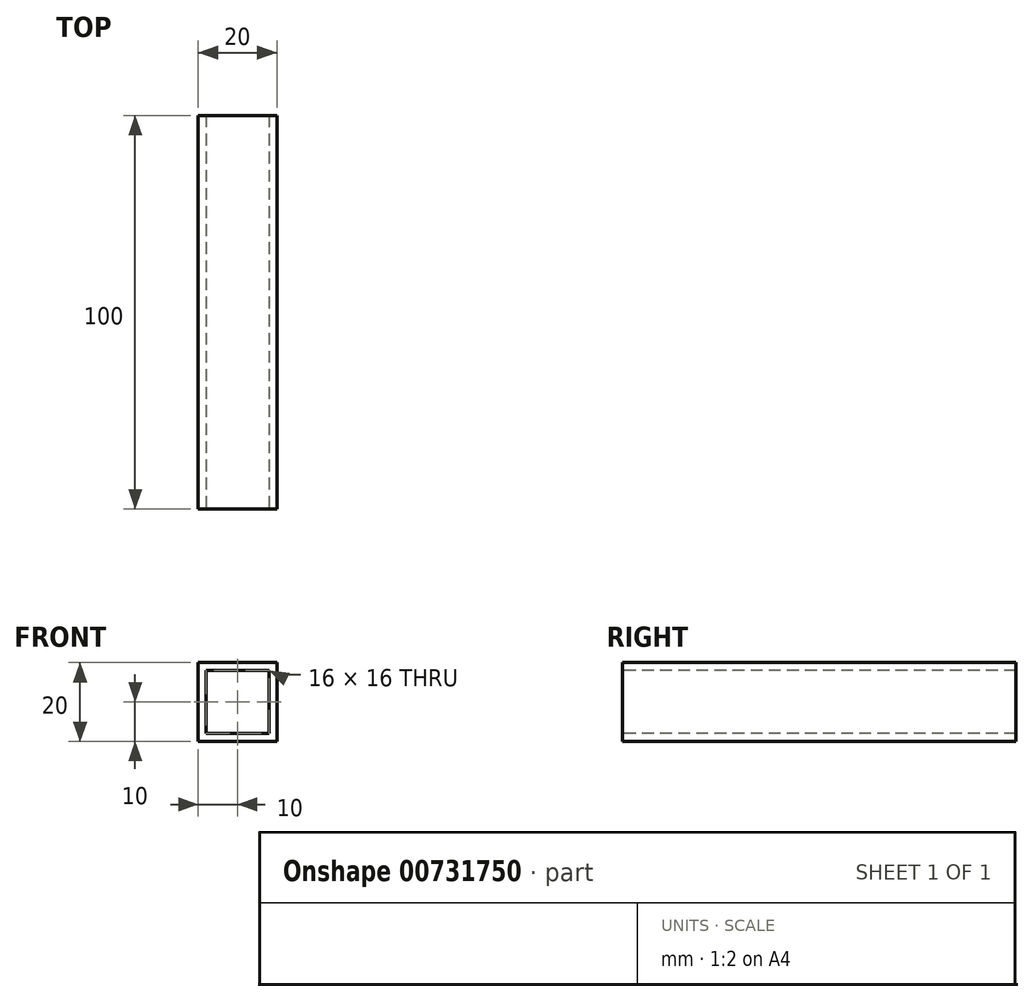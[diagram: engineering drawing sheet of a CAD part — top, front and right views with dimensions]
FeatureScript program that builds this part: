
annotation { "Feature Type Name" : "Feature", "Feature Type Description" : "" }
export const myFeature = defineFeature(function(context is Context, id is Id, definition is map)
    precondition{}
    {
        {
            var Q0;
            Q0=qCreatedBy(makeId("Front.planeOp"),FACE);
            var sketch = newSketch(context, id + "F0", { "sketchPlane" : qUnion([Q0])});
            skLineSegment(sketch, "E0.bottom", {"start": v(10, 10) * mm, "end": v(-10, 10) * mm});
            skLineSegment(sketch, "E0.top", {"start": v(10, -10) * mm, "end": v(-10, -10) * mm});
            skLineSegment(sketch, "E0.left", {"start": v(10, 10) * mm, "end": v(10, -10) * mm});
            skLineSegment(sketch, "E0.right", {"start": v(-10, 10) * mm, "end": v(-10, -10) * mm});
            skPoint(sketch, "E0.middle", {"position": v(0, 0) * mm});
            skLineSegment(sketch, "E1.0", {"start": v(8, 8) * mm, "end": v(-8, 8) * mm});
            skLineSegment(sketch, "E1.1", {"start": v(8, 8) * mm, "end": v(8, -8) * mm});
            skLineSegment(sketch, "E1.2", {"start": v(8, -8) * mm, "end": v(-8, -8) * mm});
            skLineSegment(sketch, "E1.3", {"start": v(-8, 8) * mm, "end": v(-8, -8) * mm});
            skSolve(sketch);
        }
        {
            var Q0;
            Q0=makeQuery(id+"F0.imprint","IMPRINT",FACE,{"disambiguationData":[TD([[makeQuery(id+"F0.imprint","IMPRINT",EDGE,{"derivedFrom":sQuery(id+"F0.wireOp",EDGE,"E0.bottom")}),1.0]])]});
            extrude(context, id + "F1", {"entities" : qUnion([Q0]), "oppositeDirection" : true, "depth" : 100 * mm, "offsetDistance" : 25 * mm});
        }
    });
